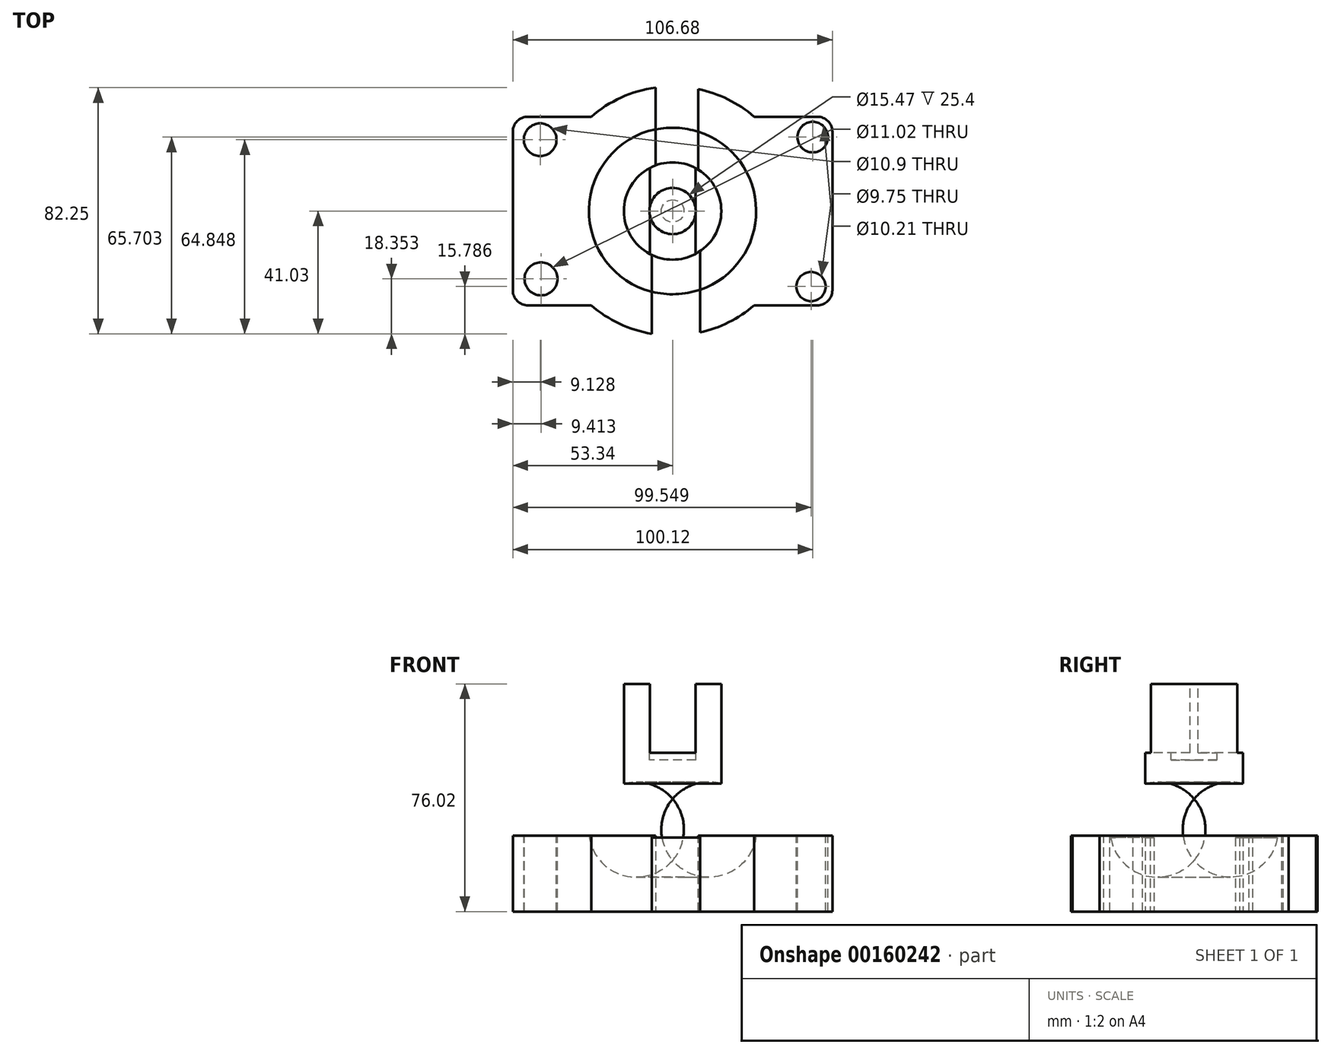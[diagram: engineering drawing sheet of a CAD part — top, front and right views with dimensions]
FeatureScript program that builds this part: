
annotation { "Feature Type Name" : "Feature", "Feature Type Description" : "" }
export const myFeature = defineFeature(function(context is Context, id is Id, definition is map)
    precondition{}
    {
        {
            var Q0;
            Q0=qCreatedBy(makeId("Top.planeOp"),FACE);
            var sketch = newSketch(context, id + "F0", { "sketchPlane" : qUnion([Q0])});
            skLineSegment(sketch, "E0.bottom", {"start": v(53.34, -31.52) * mm, "end": v(-53.34, -31.52) * mm});
            skLineSegment(sketch, "E0.top", {"start": v(53.34, 31.52) * mm, "end": v(-53.34, 31.52) * mm});
            skLineSegment(sketch, "E0.left", {"start": v(53.34, -31.52) * mm, "end": v(53.34, 31.52) * mm});
            skLineSegment(sketch, "E0.right", {"start": v(-53.34, -31.52) * mm, "end": v(-53.34, 31.52) * mm});
            skPoint(sketch, "E0.middle", {"position": v(0, 0) * mm});
            skCircle(sketch, "E1", {"center": v(0, 0) * mm, "radius": 41.62 * mm});
            skSolve(sketch);
        }
        {
            var Q0;
            {var subQ0=sQuery(id+"F0.wireOp",EDGE,"E0.right");Q0=makeQuery(id+"F0.imprint","IMPRINT",FACE,{"disambiguationData":[TD([[makeQuery(id+"F0.imprint","IMPRINT",EDGE,{"derivedFrom":subQ0}),-1.0]])]});}
            var Q1;
            {var subQ0=sQuery(id+"F0.wireOp",EDGE,"E0.left");Q1=makeQuery(id+"F0.imprint","IMPRINT",FACE,{"disambiguationData":[TD([[makeQuery(id+"F0.imprint","IMPRINT",EDGE,{"derivedFrom":subQ0}),1.0]])]});}
            var Q2;
            {var subQ0=sQuery(id+"F0.wireOp",EDGE,"E1");var subQ1=sQuery(id+"F0.wireOp",EDGE,"E0.bottom");var subQ2=makeQuery(id+"F0.imprint","INTERSECT",VERTEX,{"disambiguationData":[OD(0.0)],"derivedFrom":[subQ1,subQ0]});Q2=makeQuery(id+"F0.imprint","IMPRINT",FACE,{"disambiguationData":[TD([[makeQuery(id+"F0.imprint","IMPRINT",EDGE,{"disambiguationData":[TD([[subQ2,-1.0]])],"derivedFrom":subQ1}),1.0]])]});}
            var Q3;
            {var subQ0=sQuery(id+"F0.wireOp",EDGE,"E1");var subQ1=sQuery(id+"F0.wireOp",EDGE,"E0.top");var subQ2=makeQuery(id+"F0.imprint","INTERSECT",VERTEX,{"disambiguationData":[OD(0.0)],"derivedFrom":[subQ1,subQ0]});Q3=makeQuery(id+"F0.imprint","IMPRINT",FACE,{"disambiguationData":[TD([[makeQuery(id+"F0.imprint","IMPRINT",EDGE,{"disambiguationData":[TD([[subQ2,-1.0]])],"derivedFrom":subQ1}),-1.0]])]});}
            var Q4;
            {var subQ0=sQuery(id+"F0.wireOp",EDGE,"E1");var subQ1=sQuery(id+"F0.wireOp",EDGE,"E0.bottom");var subQ2=makeQuery(id+"F0.imprint","INTERSECT",VERTEX,{"disambiguationData":[OD(0.0)],"derivedFrom":[subQ1,subQ0]});Q4=makeQuery(id+"F0.imprint","IMPRINT",FACE,{"disambiguationData":[TD([[makeQuery(id+"F0.imprint","IMPRINT",EDGE,{"disambiguationData":[TD([[subQ2,-1.0]])],"derivedFrom":subQ1}),-1.0]])]});}
            extrude(context, id + "F1", {"entities" : qUnion([Q0, Q1, Q2, Q3, Q4]), "depth" : 25.4 * mm});
        }
        {
            var Q0;
            Q0=makeQuery(id+"F1.opExtrude","CAP_FACE",FACE,{"disambiguationData":[OSD([sQuery(id+"F0.wireOp",EDGE,"E0.bottom"),sQuery(id+"F0.wireOp",EDGE,"E0.top"),sQuery(id+"F0.wireOp",EDGE,"E0.left"),sQuery(id+"F0.wireOp",EDGE,"E0.right"),sQuery(id+"F0.wireOp",EDGE,"E1")])],"isStart":false});
            var sketch = newSketch(context, id + "F2", { "sketchPlane" : qUnion([Q0])});
            skCircle(sketch, "E2", {"center": v(-43.93, -22.68) * mm, "radius": 5.5 * mm});
            skCircle(sketch, "E3", {"center": v(-44.21, 23.82) * mm, "radius": 5.45 * mm});
            skSolve(sketch);
        }
        {
            var Q0;
            Q0=makeQuery(id+"F2.imprint","IMPRINT",FACE,{"disambiguationData":[TD([[makeQuery(id+"F2.imprint","IMPRINT",EDGE,{"derivedFrom":sQuery(id+"F2.wireOp",EDGE,"E3")}),1.0]])]});
            var Q1;
            Q1=makeQuery(id+"F2.imprint","IMPRINT",FACE,{"disambiguationData":[TD([[makeQuery(id+"F2.imprint","IMPRINT",EDGE,{"derivedFrom":sQuery(id+"F2.wireOp",EDGE,"E2")}),1.0]])]});
            var Q2;
            Q2=sQuery(id+"F2.wireOp",EDGE,"E2");
            var Q3;
            Q3=sQuery(id+"F2.wireOp",EDGE,"E3");
            extrude(context, id + "F3", {"entities" : qUnion([Q0, Q1]), "operationType" : NewBodyOperationType.REMOVE, "surfaceEntities" : qUnion([Q2, Q3]), "oppositeDirection" : true, "depth" : 25.4 * mm});
        }
        {
            var Q0;
            Q0=makeQuery(id+"F1.opExtrude","CAP_FACE",FACE,{"disambiguationData":[OSD([sQuery(id+"F0.wireOp",EDGE,"E0.bottom"),sQuery(id+"F0.wireOp",EDGE,"E0.top"),sQuery(id+"F0.wireOp",EDGE,"E0.left"),sQuery(id+"F0.wireOp",EDGE,"E0.right"),sQuery(id+"F0.wireOp",EDGE,"E1")])],"isStart":false});
            var sketch = newSketch(context, id + "F4", { "sketchPlane" : qUnion([Q0])});
            skCircle(sketch, "E4", {"center": v(46.78, 24.67) * mm, "radius": 5.1 * mm});
            skCircle(sketch, "E5", {"center": v(46.2, -25.24) * mm, "radius": 4.87 * mm});
            skSolve(sketch);
        }
        {
            var Q0;
            Q0=makeQuery(id+"F4.imprint","IMPRINT",FACE,{"disambiguationData":[TD([[makeQuery(id+"F4.imprint","IMPRINT",EDGE,{"derivedFrom":sQuery(id+"F4.wireOp",EDGE,"E4")}),1.0]])]});
            var Q1;
            Q1=makeQuery(id+"F4.imprint","IMPRINT",FACE,{"disambiguationData":[TD([[makeQuery(id+"F4.imprint","IMPRINT",EDGE,{"derivedFrom":sQuery(id+"F4.wireOp",EDGE,"E5")}),1.0]])]});
            extrude(context, id + "F5", {"entities" : qUnion([Q0, Q1]), "operationType" : NewBodyOperationType.REMOVE, "oppositeDirection" : true, "depth" : 25.4 * mm});
        }
        {
            var Q0;
            Q0=makeQuery(id+"F1.opExtrude","CAP_FACE",FACE,{"disambiguationData":[OSD([sQuery(id+"F0.wireOp",EDGE,"E0.bottom"),sQuery(id+"F0.wireOp",EDGE,"E0.top"),sQuery(id+"F0.wireOp",EDGE,"E0.left"),sQuery(id+"F0.wireOp",EDGE,"E0.right"),sQuery(id+"F0.wireOp",EDGE,"E1")])],"isStart":false});
            var sketch = newSketch(context, id + "F6", { "sketchPlane" : qUnion([Q0])});
            skLineSegment(sketch, "E6.bottom", {"start": v(-6.99, -41.03) * mm, "end": v(9.13, -41.03) * mm});
            skLineSegment(sketch, "E6.top", {"start": v(-6.99, -11.55) * mm, "end": v(9.13, -11.55) * mm});
            skLineSegment(sketch, "E6.left", {"start": v(-6.99, -41.03) * mm, "end": v(-6.99, -11.55) * mm});
            skLineSegment(sketch, "E6.right", {"start": v(9.13, -41.03) * mm, "end": v(9.13, -11.55) * mm});
            skLineSegment(sketch, "E7.bottom", {"start": v(-5.74, 41.22) * mm, "end": v(8.56, 41.22) * mm});
            skLineSegment(sketch, "E7.top", {"start": v(-5.74, 11.27) * mm, "end": v(8.56, 11.27) * mm});
            skLineSegment(sketch, "E7.left", {"start": v(-5.74, 41.22) * mm, "end": v(-5.74, 11.27) * mm});
            skLineSegment(sketch, "E7.right", {"start": v(8.56, 41.22) * mm, "end": v(8.56, 11.27) * mm});
            skSolve(sketch);
        }
        {
            var Q0;
            {var subQ1=sQuery(id+"F6.wireOp",EDGE,"E7.top");Q0=makeQuery(id+"F6.imprint","IMPRINT",FACE,{"disambiguationData":[TD([[makeQuery(id+"F6.imprint","IMPRINT",EDGE,{"derivedFrom":subQ1}),1.0]])]});}
            var Q1;
            {var subQ1=sQuery(id+"F6.wireOp",EDGE,"E6.top");Q1=makeQuery(id+"F6.imprint","IMPRINT",FACE,{"disambiguationData":[TD([[makeQuery(id+"F6.imprint","IMPRINT",EDGE,{"derivedFrom":subQ1}),-1.0]])]});}
            extrude(context, id + "F7", {"entities" : qUnion([Q0, Q1]), "operationType" : NewBodyOperationType.REMOVE, "oppositeDirection" : true, "depth" : 25.4 * mm});
        }
        {
            var Q0;
            {var subQ0=sQuery(id+"F0.wireOp",EDGE,"E1");var subQ1=sQuery(id+"F0.wireOp",EDGE,"E0.bottom");Q0=makeQuery(id+"F7.boolean.opBoolean","SPLIT",FACE,{"disambiguationData":[TD([makeQuery(id+"F7.opExtrude","SWEPT_FACE",FACE,{"disambiguationData":[OSD([sQuery(id+"F6.wireOp",EDGE,"E6.bottom")])]})])],"derivedFrom":makeQuery(id+"F1.opExtrude","CAP_FACE",FACE,{"disambiguationData":[OSD([subQ1,sQuery(id+"F0.wireOp",EDGE,"E0.top"),sQuery(id+"F0.wireOp",EDGE,"E0.left"),sQuery(id+"F0.wireOp",EDGE,"E0.right"),subQ0])],"isStart":false})});}
            extrude(context, id + "F8", {"entities" : qUnion([Q0]), "operationType" : NewBodyOperationType.REMOVE, "oppositeDirection" : true, "depth" : 25.4 * mm});
        }
        {
            var Q0;
            Q0=makeQuery(id+"F7.boolean.opBoolean","COPY",FACE,{"derivedFrom":makeQuery(id+"F7.opExtrude","SWEPT_FACE",FACE,{"disambiguationData":[OSD([sQuery(id+"F6.wireOp",EDGE,"E7.bottom")])]})});
            extrude(context, id + "F9", {"entities" : qUnion([Q0]), "operationType" : NewBodyOperationType.REMOVE, "oppositeDirection" : true, "depth" : 25.4 * mm});
        }
        {
            var Q0;
            Q0=makeQuery(id+"F1.opExtrude","SWEPT_EDGE",EDGE,{"disambiguationData":[OSD([sQuery(id+"F0.wireOp",EDGE,"E0.bottom"),sQuery(id+"F0.wireOp",EDGE,"E0.left")])]});
            var Q1;
            Q1=makeQuery(id+"F1.opExtrude","SWEPT_EDGE",EDGE,{"disambiguationData":[OSD([sQuery(id+"F0.wireOp",EDGE,"E0.top"),sQuery(id+"F0.wireOp",EDGE,"E0.left")])]});
            var Q2;
            Q2=makeQuery(id+"F1.opExtrude","SWEPT_EDGE",EDGE,{"disambiguationData":[OSD([sQuery(id+"F0.wireOp",EDGE,"E0.bottom"),sQuery(id+"F0.wireOp",EDGE,"E0.right")])]});
            var Q3;
            Q3=makeQuery(id+"F1.opExtrude","SWEPT_EDGE",EDGE,{"disambiguationData":[OSD([sQuery(id+"F0.wireOp",EDGE,"E0.top"),sQuery(id+"F0.wireOp",EDGE,"E0.right")])]});
            fillet(context, id + "F10", {"entities" : qUnion([Q0, Q1, Q2, Q3]), "radius" : 5.08 * mm, "tangentPropagation" : true, "allowEdgeOverflow" : false});
        }
        {
            var Q0;
            Q0=qCreatedBy(makeId("Front.planeOp"),FACE);
            var sketch = newSketch(context, id + "F11", { "sketchPlane" : qUnion([Q0])});
            skLineSegment(sketch, "E8.bottom", {"start": v(0, 0) * mm, "end": v(-16.26, 0) * mm});
            skLineSegment(sketch, "E8.top", {"start": v(0, 76.02) * mm, "end": v(-16.26, 76.02) * mm});
            skLineSegment(sketch, "E8.left", {"start": v(0, 0) * mm, "end": v(0, 76.02) * mm});
            skLineSegment(sketch, "E8.right", {"start": v(-16.26, 0) * mm, "end": v(-16.26, 76.02) * mm});
            skLineSegment(sketch, "E9", {"start": v(-16.26, 24.74) * mm, "end": v(-27.81, 24.74) * mm});
            skArc(sketch, "E10", {"start": v(-16.26, 42.71) * mm, "mid": v(-25.5, 35.96) * mm, "end": v(-27.81, 24.74) * mm});
            skSolve(sketch);
        }
        {
            var Q0;
            Q0=makeQuery(id+"F11.imprint","IMPRINT",FACE,{"disambiguationData":[TD([[makeQuery(id+"F11.imprint","IMPRINT",EDGE,{"derivedFrom":sQuery(id+"F11.wireOp",EDGE,"E8.bottom")}),-1.0]])]});
            var Q1;
            Q1=sQuery(id+"F11.wireOp",EDGE,"E8.left");
            revolve(context, id + "F12", {"operationType" : NewBodyOperationType.ADD, "entities" : qUnion([Q0]), "axis" : qUnion([Q1]), "revolveType" : RevolveType.FULL});
        }
        {
            var Q0;
            Q0 = qSketchRegion(id + "F11", true);
            var Q1;
            Q1=makeQuery(id+"F12.opRevolve","SWEPT_FACE",FACE,{"disambiguationData":[OSD([sQuery(id+"F11.wireOp",EDGE,"E8.right")])]});
            revolve(context, id + "F13", {"operationType" : NewBodyOperationType.ADD, "entities" : qUnion([Q0]), "axis" : qUnion([Q1]), "revolveType" : RevolveType.FULL});
        }
        {
            var Q0;
            Q0=makeQuery(id+"F12.opRevolve","SWEPT_FACE",FACE,{"disambiguationData":[OSD([sQuery(id+"F11.wireOp",EDGE,"E8.top")])]});
            var sketch = newSketch(context, id + "F14", { "sketchPlane" : qUnion([Q0])});
            skSolve(sketch);
        }
        {
            var Q0;
            Q0=makeQuery(id+"F14.imprint","IMPRINT",FACE,{"disambiguationData":[TD([[makeQuery(id+"F14.imprint","IMPRINT",EDGE,{"derivedFrom":makeQuery(id+"F12.opRevolve","SWEPT_EDGE",EDGE,{"disambiguationData":[OSD([sQuery(id+"F11.wireOp",EDGE,"E8.top"),sQuery(id+"F11.wireOp",EDGE,"E8.right")])]})}),-1.0]])]});
            var sketch = newSketch(context, id + "F15", { "sketchPlane" : qUnion([Q0])});
            skCircle(sketch, "E11", {"center": v(0, 0) * mm, "radius": 7.73 * mm});
            skSolve(sketch);
        }
        {
            var Q0;
            Q0 = qSketchRegion(id + "F15", true);
            extrude(context, id + "F16", {"entities" : qUnion([Q0]), "operationType" : NewBodyOperationType.REMOVE, "oppositeDirection" : true, "depth" : 25.4 * mm});
        }
        {
            var Q0;
            Q0=qCreatedBy(makeId("Front.planeOp"),FACE);
            var sketch = newSketch(context, id + "F17", { "sketchPlane" : qUnion([Q0])});
            skLineSegment(sketch, "E12.top", {"start": v(-7.62, 86.86) * mm, "end": v(7.62, 86.86) * mm});
            skLineSegment(sketch, "E12.left", {"start": v(-7.62, 53.05) * mm, "end": v(-7.62, 86.86) * mm});
            skLineSegment(sketch, "E12.right", {"start": v(7.62, 53.05) * mm, "end": v(7.62, 86.86) * mm});
            skLineSegment(sketch, "E13", {"start": v(-7.62, 53.05) * mm, "end": v(7.62, 53.05) * mm});
            skSolve(sketch);
        }
        {
            var Q0;
            Q0=makeQuery(id+"F17.imprint","IMPRINT",FACE,{"disambiguationData":[TD([[makeQuery(id+"F17.imprint","IMPRINT",EDGE,{"derivedFrom":sQuery(id+"F17.wireOp",EDGE,"E12.top")}),-1.0]])]});
            extrude(context, id + "F18", {"entities" : qUnion([Q0]), "operationType" : NewBodyOperationType.REMOVE, "oppositeDirection" : true, "depth" : 25.4 * mm, "hasSecondDirection" : true, "secondDirectionOppositeDirection" : false, "secondDirectionDepth" : 25.4 * mm});
        }
    });
